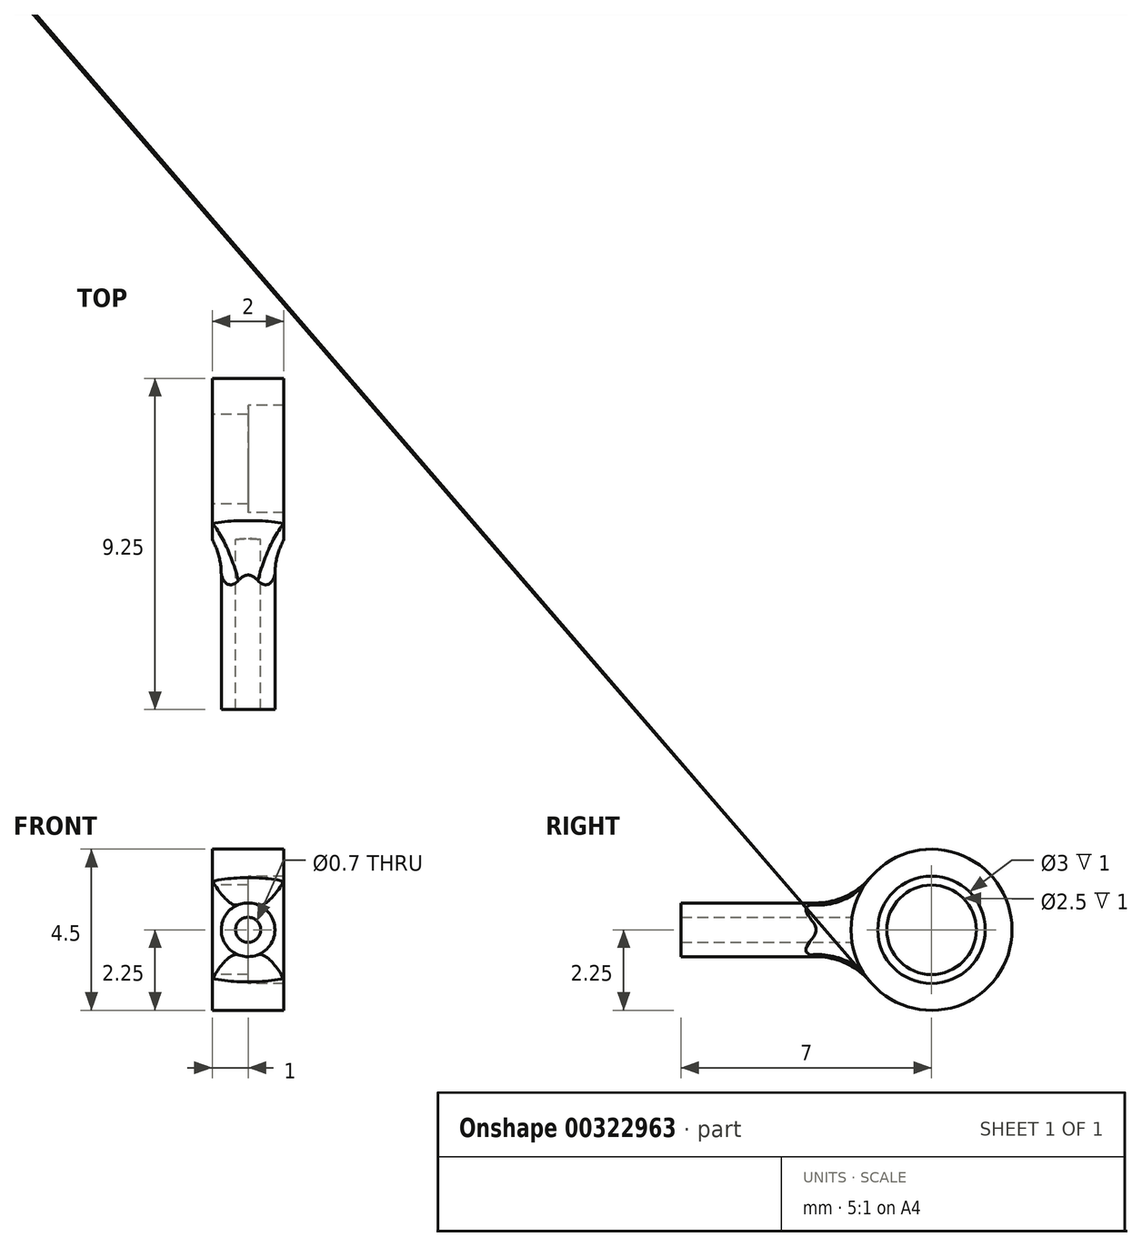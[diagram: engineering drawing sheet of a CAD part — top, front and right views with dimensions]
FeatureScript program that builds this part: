
annotation { "Feature Type Name" : "Feature", "Feature Type Description" : "" }
export const myFeature = defineFeature(function(context is Context, id is Id, definition is map)
    precondition{}
    {
        {
            var Q0;
            Q0=qCreatedBy(makeId("Front.planeOp"),FACE);
            var sketch = newSketch(context, id + "F0", { "sketchPlane" : qUnion([Q0])});
            skLineSegment(sketch, "E0", {"start": v(0, 0) * mm, "end": v(1, 0) * mm, "construction": true});
            skCircle(sketch, "E1", {"center": v(1, 0) * mm, "radius": 0.75 * mm});
            skCircle(sketch, "E2", {"center": v(1, 0) * mm, "radius": 0.35 * mm});
            skSolve(sketch);
        }
        {
            var Q0;
            Q0 = qSketchRegion(id + "F0", true);
            extrude(context, id + "F1", {"entities" : qUnion([Q0]), "depth" : 7 * mm});
        }
        {
            var Q0;
            Q0=qCreatedBy(makeId("Right.planeOp"),FACE);
            var sketch = newSketch(context, id + "F2", { "sketchPlane" : qUnion([Q0])});
            skCircle(sketch, "E3", {"center": v(0, 0) * mm, "radius": 1.5 * mm});
            skCircle(sketch, "E4", {"center": v(0, 0) * mm, "radius": 2.25 * mm});
            skSolve(sketch);
        }
        {
            var Q0;
            Q0=makeQuery(id+"F2.imprint","IMPRINT",FACE,{"disambiguationData":[TD([[makeQuery(id+"F2.imprint","IMPRINT",EDGE,{"derivedFrom":sQuery(id+"F2.wireOp",EDGE,"E3")}),1.0]])]});
            extrude(context, id + "F3", {"entities" : qUnion([Q0]), "operationType" : NewBodyOperationType.REMOVE, "depth" : 2 * mm});
        }
        {
            var Q0;
            Q0=qCreatedBy(makeId("Right.planeOp"),FACE);
            var sketch = newSketch(context, id + "F4", { "sketchPlane" : qUnion([Q0])});
            skCircle(sketch, "E5", {"center": v(0, 0) * mm, "radius": 1.5 * mm});
            skCircle(sketch, "E6", {"center": v(0, 0) * mm, "radius": 2.25 * mm});
            skCircle(sketch, "E7", {"center": v(0, 0) * mm, "radius": 1.25 * mm});
            skSolve(sketch);
        }
        {
            var Q0;
            Q0=makeQuery(id+"F4.imprint","IMPRINT",FACE,{"disambiguationData":[TD([[makeQuery(id+"F4.imprint","IMPRINT",EDGE,{"derivedFrom":sQuery(id+"F4.wireOp",EDGE,"E5")}),1.0]])]});
            extrude(context, id + "F5", {"entities" : qUnion([Q0]), "operationType" : NewBodyOperationType.ADD, "depth" : 1 * mm});
        }
        {
            var Q0;
            Q0 = qSketchRegion(id + "F4", true);
            extrude(context, id + "F6", {"entities" : qUnion([Q0]), "operationType" : NewBodyOperationType.ADD, "depth" : 2 * mm});
        }
        {
            var Q0;
            Q0=makeQuery(id+"F6.boolean.opBoolean","INTERSECT",EDGE,{"derivedFrom":[makeQuery(id+"F1.opExtrude","SWEPT_FACE",FACE,{"disambiguationData":[OSD([sQuery(id+"F0.wireOp",EDGE,"E1")])]}),makeQuery(id+"F6.opExtrude","SWEPT_FACE",FACE,{"disambiguationData":[OSD([sQuery(id+"F4.wireOp",EDGE,"E6")])]})]});
            fillet(context, id + "F7", {"entities" : qUnion([Q0]), "radius" : 2 * mm, "tangentPropagation" : true, "allowEdgeOverflow" : false});
        }
    });
